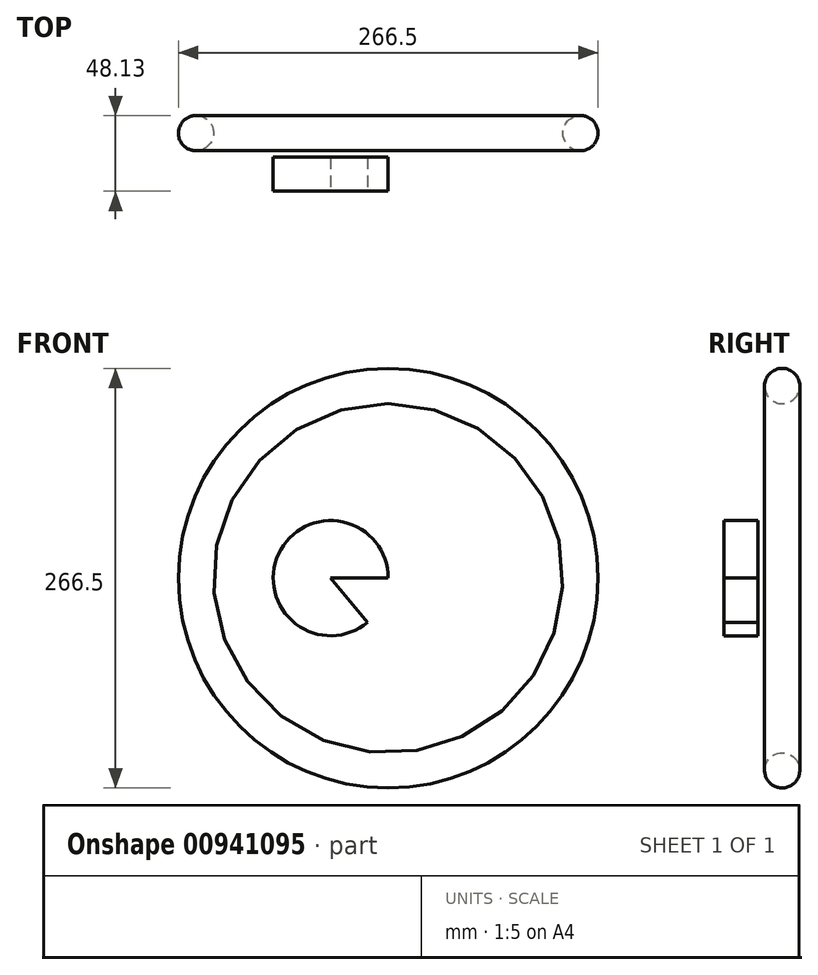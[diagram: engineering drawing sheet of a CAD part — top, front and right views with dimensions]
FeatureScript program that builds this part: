
annotation { "Feature Type Name" : "Feature", "Feature Type Description" : "" }
export const myFeature = defineFeature(function(context is Context, id is Id, definition is map)
    precondition{}
    {
        {
            var Q0;
            Q0=qCreatedBy(makeId("Top.planeOp"),FACE);
            var sketch = newSketch(context, id + "F0", { "sketchPlane" : qUnion([Q0])});
            skCircle(sketch, "E0", {"center": v(-62.28, 52.52) * mm, "radius": 11.18 * mm});
            skLineSegment(sketch, "E1.bottom", {"start": v(23.25, 37.16) * mm, "end": v(59.79, 37.16) * mm});
            skLineSegment(sketch, "E1.top", {"start": v(23.25, 15.57) * mm, "end": v(59.79, 15.57) * mm});
            skLineSegment(sketch, "E1.left", {"start": v(23.25, 37.16) * mm, "end": v(23.25, 15.57) * mm});
            skLineSegment(sketch, "E1.right", {"start": v(59.79, 37.16) * mm, "end": v(59.79, 15.57) * mm});
            skLineSegment(sketch, "E2", {"start": v(-55, -17.45) * mm, "end": v(-20.95, -29.08) * mm});
            skLineSegment(sketch, "E3", {"start": v(-20.95, -29.08) * mm, "end": v(-20.95, -63.13) * mm});
            skLineSegment(sketch, "E4", {"start": v(-20.95, -63.13) * mm, "end": v(-59.98, -69.35) * mm});
            skLineSegment(sketch, "E5", {"start": v(-59.98, -69.35) * mm, "end": v(-55, -17.45) * mm});
            skLineSegment(sketch, "E6", {"start": v(-44.62, -31.99) * mm, "end": v(-50.43, -55.24) * mm});
            skLineSegment(sketch, "E7", {"start": v(-50.43, -55.24) * mm, "end": v(-37.93, -58.36) * mm});
            skLineSegment(sketch, "E8", {"start": v(-37.93, -58.36) * mm, "end": v(-44.62, -31.99) * mm});
            skLineSegment(sketch, "E9", {"start": v(-82.91, 71.7) * mm, "end": v(-82.91, 30.26) * mm, "construction": true});
            skSolve(sketch);
        }
        {
            var Q0;
            Q0=makeQuery(id+"F0.imprint","IMPRINT",FACE,{"disambiguationData":[TD([[makeQuery(id+"F0.imprint","IMPRINT",EDGE,{"derivedFrom":sQuery(id+"F0.wireOp",EDGE,"E1.bottom")}),-1.0]])]});
            var Q1;
            Q1=sQuery(id+"F0.wireOp",EDGE,"E1.left");
            revolve(context, id + "F1", {"surfaceOperationType" : NewSurfaceOperationType.NEW, "entities" : qUnion([Q0]), "axis" : qUnion([Q1]), "revolveType" : RevolveType.ONE_DIRECTION, "angle" : 310 * degree});
        }
        {
            var Q0;
            Q0=makeQuery(id+"F0.imprint","IMPRINT",FACE,{"disambiguationData":[TD([[makeQuery(id+"F0.imprint","IMPRINT",EDGE,{"derivedFrom":sQuery(id+"F0.wireOp",EDGE,"E0")}),1.0]])]});
            var Q1;
            Q1=sQuery(id+"F0.wireOp",EDGE,"E1.right");
            revolve(context, id + "F2", {"surfaceOperationType" : NewSurfaceOperationType.NEW, "entities" : qUnion([Q0]), "axis" : qUnion([Q1]), "revolveType" : RevolveType.ONE_DIRECTION, "angle" : 360 * degree});
        }
    });
